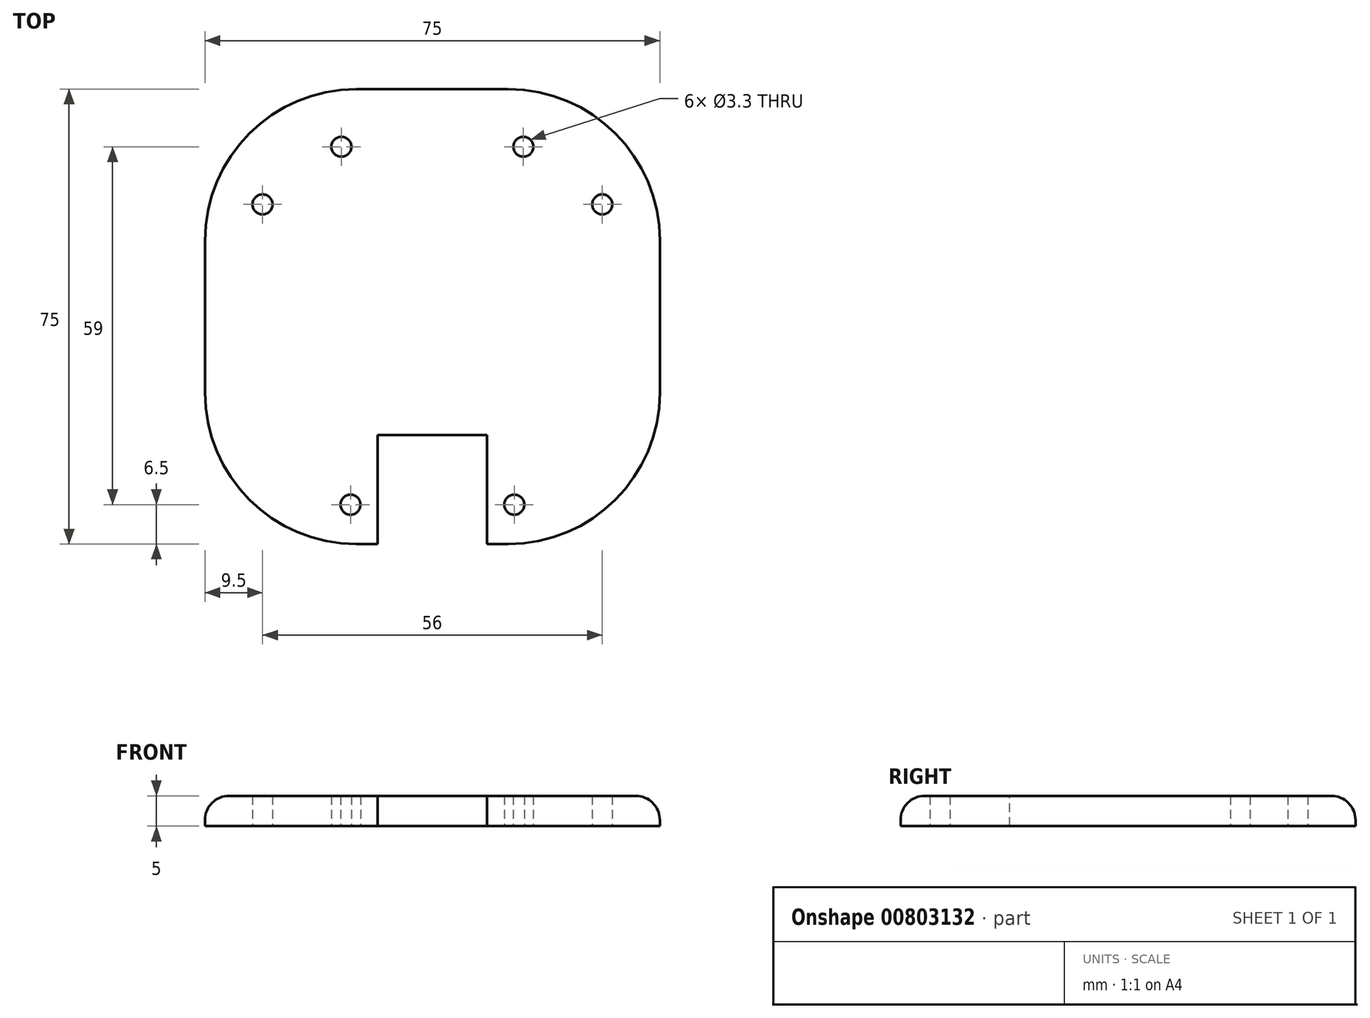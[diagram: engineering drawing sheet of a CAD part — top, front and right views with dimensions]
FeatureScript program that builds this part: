
annotation { "Feature Type Name" : "Feature", "Feature Type Description" : "" }
export const myFeature = defineFeature(function(context is Context, id is Id, definition is map)
    precondition{}
    {
        {
            var Q0;
            Q0=qCreatedBy(makeId("Top.planeOp"),FACE);
            var sketch = newSketch(context, id + "F0", { "sketchPlane" : qUnion([Q0])});
            skLineSegment(sketch, "E0.bottom", {"start": v(-12.5, 37.5) * mm, "end": v(12.5, 37.5) * mm});
            skLineSegment(sketch, "E0.top", {"start": v(-12.5, -37.5) * mm, "end": v(12.5, -37.5) * mm});
            skLineSegment(sketch, "E0.left", {"start": v(-37.5, 12.5) * mm, "end": v(-37.5, -12.5) * mm});
            skLineSegment(sketch, "E0.right", {"start": v(37.5, 12.5) * mm, "end": v(37.5, -12.5) * mm});
            skPoint(sketch, "E0.middle", {"position": v(0, 0) * mm});
            skPoint(sketch, "E1.visualSharp", {"position": v(-37.5, -37.5) * mm});
            skArc(sketch, "E1.filletArc", {"start": v(-37.5, -12.5) * mm, "mid": v(-30.18, -30.18) * mm, "end": v(-12.5, -37.5) * mm});
            skPoint(sketch, "E2.visualSharp", {"position": v(37.5, -37.5) * mm});
            skArc(sketch, "E2.filletArc", {"start": v(12.5, -37.5) * mm, "mid": v(30.18, -30.18) * mm, "end": v(37.5, -12.5) * mm});
            skPoint(sketch, "E3.visualSharp", {"position": v(37.5, 37.5) * mm});
            skArc(sketch, "E3.filletArc", {"start": v(37.5, 12.5) * mm, "mid": v(30.18, 30.18) * mm, "end": v(12.5, 37.5) * mm});
            skPoint(sketch, "E4.visualSharp", {"position": v(-37.5, 37.5) * mm});
            skArc(sketch, "E4.filletArc", {"start": v(-12.5, 37.5) * mm, "mid": v(-30.18, 30.18) * mm, "end": v(-37.5, 12.5) * mm});
            skLineSegment(sketch, "E5", {"start": v(-44.4, 0) * mm, "end": v(56.5, 0) * mm, "construction": true});
            skLineSegment(sketch, "E6", {"start": v(0, 45.34) * mm, "end": v(0, -46.86) * mm, "construction": true});
            skPoint(sketch, "E6.endSnap0", {"position": v(0, -37.5) * mm});
            skSolve(sketch);
        }
        {
            var Q0;
            Q0=makeQuery(id+"F0.imprint","IMPRINT",FACE,{"disambiguationData":[TD([[makeQuery(id+"F0.imprint","IMPRINT",EDGE,{"derivedFrom":sQuery(id+"F0.wireOp",EDGE,"E0.bottom")}),-1.0]])]});
            extrude(context, id + "F1", {"entities" : qUnion([Q0]), "depth" : 5 * mm, "offsetDistance" : 25 * mm});
        }
        {
            var Q0;
            Q0=makeQuery(id+"F1.opExtrude","CAP_FACE",FACE,{"disambiguationData":[OSD([sQuery(id+"F0.wireOp",EDGE,"E0.bottom"),sQuery(id+"F0.wireOp",EDGE,"E0.top"),sQuery(id+"F0.wireOp",EDGE,"E0.left"),sQuery(id+"F0.wireOp",EDGE,"E0.right"),sQuery(id+"F0.wireOp",EDGE,"E1.filletArc"),sQuery(id+"F0.wireOp",EDGE,"E2.filletArc"),sQuery(id+"F0.wireOp",EDGE,"E3.filletArc"),sQuery(id+"F0.wireOp",EDGE,"E4.filletArc")])],"isStart":false});
            fillet(context, id + "F2", {"entities" : qUnion([Q0]), "radius" : 4 * mm, "tangentPropagation" : true, "allowEdgeOverflow" : false});
        }
        {
            var Q0;
            Q0=makeQuery(id+"F1.opExtrude","CAP_FACE",FACE,{"disambiguationData":[OSD([sQuery(id+"F0.wireOp",EDGE,"E0.bottom"),sQuery(id+"F0.wireOp",EDGE,"E0.top"),sQuery(id+"F0.wireOp",EDGE,"E0.left"),sQuery(id+"F0.wireOp",EDGE,"E0.right"),sQuery(id+"F0.wireOp",EDGE,"E1.filletArc"),sQuery(id+"F0.wireOp",EDGE,"E2.filletArc"),sQuery(id+"F0.wireOp",EDGE,"E3.filletArc"),sQuery(id+"F0.wireOp",EDGE,"E4.filletArc")])],"isStart":false});
            var sketch = newSketch(context, id + "F3", { "sketchPlane" : qUnion([Q0])});
            skLineSegment(sketch, "E7", {"start": v(-78.92, 0) * mm, "end": v(95.72, 0) * mm, "construction": true});
            skLineSegment(sketch, "E8", {"start": v(0, 79.66) * mm, "end": v(0, -84.35) * mm, "construction": true});
            skLineSegment(sketch, "E9", {"start": v(-63.11, 18.5) * mm, "end": v(75.46, 18.5) * mm, "construction": true});
            skLineSegment(sketch, "E10", {"start": v(-65.83, -31) * mm, "end": v(83.12, -31) * mm, "construction": true});
            skPoint(sketch, "E11", {"position": v(-28, 18.5) * mm});
            skPoint(sketch, "E12", {"position": v(28, 18.5) * mm});
            skPoint(sketch, "E13", {"position": v(13.5, -31) * mm});
            skPoint(sketch, "E14", {"position": v(-13.5, -31) * mm});
            skSolve(sketch);
        }
        {
            var Q0;
            Q0=sQuery(id+"F3.wireOp",VERTEX,"E11");
            var Q1;
            Q1=sQuery(id+"F3.wireOp",VERTEX,"E12");
            var Q2;
            Q2=sQuery(id+"F3.wireOp",VERTEX,"E14");
            var Q3;
            Q3=sQuery(id+"F3.wireOp",VERTEX,"E13");
            var Q4;
            Q4=makeQuery(id+"F1.opExtrude","SWEPT_BODY",BODY,{"disambiguationData":[OSD([sQuery(id+"F0.wireOp",EDGE,"E0.bottom"),sQuery(id+"F0.wireOp",EDGE,"E0.top"),sQuery(id+"F0.wireOp",EDGE,"E0.left"),sQuery(id+"F0.wireOp",EDGE,"E0.right"),sQuery(id+"F0.wireOp",EDGE,"E1.filletArc"),sQuery(id+"F0.wireOp",EDGE,"E2.filletArc"),sQuery(id+"F0.wireOp",EDGE,"E3.filletArc"),sQuery(id+"F0.wireOp",EDGE,"E4.filletArc")])]});
            hole(context, id + "F4", {"style" : HoleStyle.SIMPLE, "endStyle" : HoleEndStyle.THROUGH, "standardTappedOrClearance" : lookupTablePath({ "standard" : "ISO", "engagement" : "75%", "pitch" : "0.7 mm", "size" : "M4", "type" : "Tapped" }), "standardBlindInLast" : lookupTablePath({ "standard" : "ISO", "engagement" : "75%", "pitch" : "0.7 mm", "size" : "M4", "type" : "Tapped" }), "holeDiameter" : 3.3 * mm, "majorDiameter" : 4 * mm, "showTappedDepth" : true, "isTappedThrough" : true, "tappedDepth" : 12 * mm, "tapClearance" : 3, "locations" : qUnion([Q0, Q1, Q2, Q3]), "scope" : qUnion([Q4]), "startStyle" : HoleStartStyle.PART});
        }
        {
            var Q0;
            Q0=makeQuery(id+"F1.opExtrude","CAP_FACE",FACE,{"disambiguationData":[OSD([sQuery(id+"F0.wireOp",EDGE,"E0.bottom"),sQuery(id+"F0.wireOp",EDGE,"E0.top"),sQuery(id+"F0.wireOp",EDGE,"E0.left"),sQuery(id+"F0.wireOp",EDGE,"E0.right"),sQuery(id+"F0.wireOp",EDGE,"E1.filletArc"),sQuery(id+"F0.wireOp",EDGE,"E2.filletArc"),sQuery(id+"F0.wireOp",EDGE,"E3.filletArc"),sQuery(id+"F0.wireOp",EDGE,"E4.filletArc")])],"isStart":false});
            var sketch = newSketch(context, id + "F5", { "sketchPlane" : qUnion([Q0])});
            skLineSegment(sketch, "E15.bottom", {"start": v(-9, -37.5) * mm, "end": v(9, -37.5) * mm});
            skLineSegment(sketch, "E15.top", {"start": v(-9, -19.5) * mm, "end": v(9, -19.5) * mm});
            skLineSegment(sketch, "E15.left", {"start": v(-9, -37.5) * mm, "end": v(-9, -19.5) * mm});
            skLineSegment(sketch, "E15.right", {"start": v(9, -37.5) * mm, "end": v(9, -19.5) * mm});
            skLineSegment(sketch, "E16", {"start": v(0, 42.67) * mm, "end": v(0, -51.15) * mm, "construction": true});
            skSolve(sketch);
        }
        {
            var Q0;
            Q0 = qSketchRegion(id + "F5", true);
            extrude(context, id + "F6", {"entities" : qUnion([Q0]), "operationType" : NewBodyOperationType.REMOVE, "endBound" : BoundingType.THROUGH_ALL, "oppositeDirection" : true, "depth" : 25 * mm, "offsetDistance" : 25 * mm});
        }
        {
            var Q0;
            Q0=makeQuery(id+"F1.opExtrude","CAP_FACE",FACE,{"disambiguationData":[OSD([sQuery(id+"F0.wireOp",EDGE,"E0.bottom"),sQuery(id+"F0.wireOp",EDGE,"E0.top"),sQuery(id+"F0.wireOp",EDGE,"E0.left"),sQuery(id+"F0.wireOp",EDGE,"E0.right"),sQuery(id+"F0.wireOp",EDGE,"E1.filletArc"),sQuery(id+"F0.wireOp",EDGE,"E2.filletArc"),sQuery(id+"F0.wireOp",EDGE,"E3.filletArc"),sQuery(id+"F0.wireOp",EDGE,"E4.filletArc")])],"isStart":false});
            var sketch = newSketch(context, id + "F7", { "sketchPlane" : qUnion([Q0])});
            skLineSegment(sketch, "E17", {"start": v(-40, 28) * mm, "end": v(39.72, 28) * mm, "construction": true});
            skArc(sketch, "E18", {"start": v(-15, 33) * mm, "mid": v(-20, 28) * mm, "end": v(-15, 23) * mm, "construction": true});
            skArc(sketch, "E19", {"start": v(15, 23) * mm, "mid": v(20, 28) * mm, "end": v(15, 33) * mm, "construction": true});
            skLineSegment(sketch, "E20", {"start": v(0, 46.57) * mm, "end": v(0, -40.93) * mm, "construction": true});
            skLineSegment(sketch, "E21", {"start": v(-15, 33) * mm, "end": v(15, 33) * mm, "construction": true});
            skLineSegment(sketch, "E22", {"start": v(-15, 23) * mm, "end": v(15, 23) * mm, "construction": true});
            skSolve(sketch);
        }
        {
            var Q0;
            Q0=sQuery(id+"F7.wireOp",VERTEX,"E18.center");
            var Q1;
            Q1=sQuery(id+"F7.wireOp",VERTEX,"E19.center");
            var Q2;
            Q2=makeQuery(id+"F1.opExtrude","SWEPT_BODY",BODY,{"disambiguationData":[OSD([sQuery(id+"F0.wireOp",EDGE,"E0.bottom"),sQuery(id+"F0.wireOp",EDGE,"E0.top"),sQuery(id+"F0.wireOp",EDGE,"E0.left"),sQuery(id+"F0.wireOp",EDGE,"E0.right"),sQuery(id+"F0.wireOp",EDGE,"E1.filletArc"),sQuery(id+"F0.wireOp",EDGE,"E2.filletArc"),sQuery(id+"F0.wireOp",EDGE,"E3.filletArc"),sQuery(id+"F0.wireOp",EDGE,"E4.filletArc")])]});
            hole(context, id + "F8", {"style" : HoleStyle.SIMPLE, "endStyle" : HoleEndStyle.THROUGH, "standardTappedOrClearance" : lookupTablePath({ "standard" : "ISO", "engagement" : "75%", "pitch" : "0.7 mm", "size" : "M4", "type" : "Tapped" }), "standardBlindInLast" : lookupTablePath({ "standard" : "ISO", "engagement" : "75%", "pitch" : "0.7 mm", "size" : "M4", "type" : "Tapped" }), "holeDiameter" : 3.3 * mm, "majorDiameter" : 4 * mm, "showTappedDepth" : true, "isTappedThrough" : true, "tappedDepth" : 12 * mm, "tapClearance" : 3, "locations" : qUnion([Q0, Q1]), "scope" : qUnion([Q2]), "startStyle" : HoleStartStyle.PART});
        }
    });
